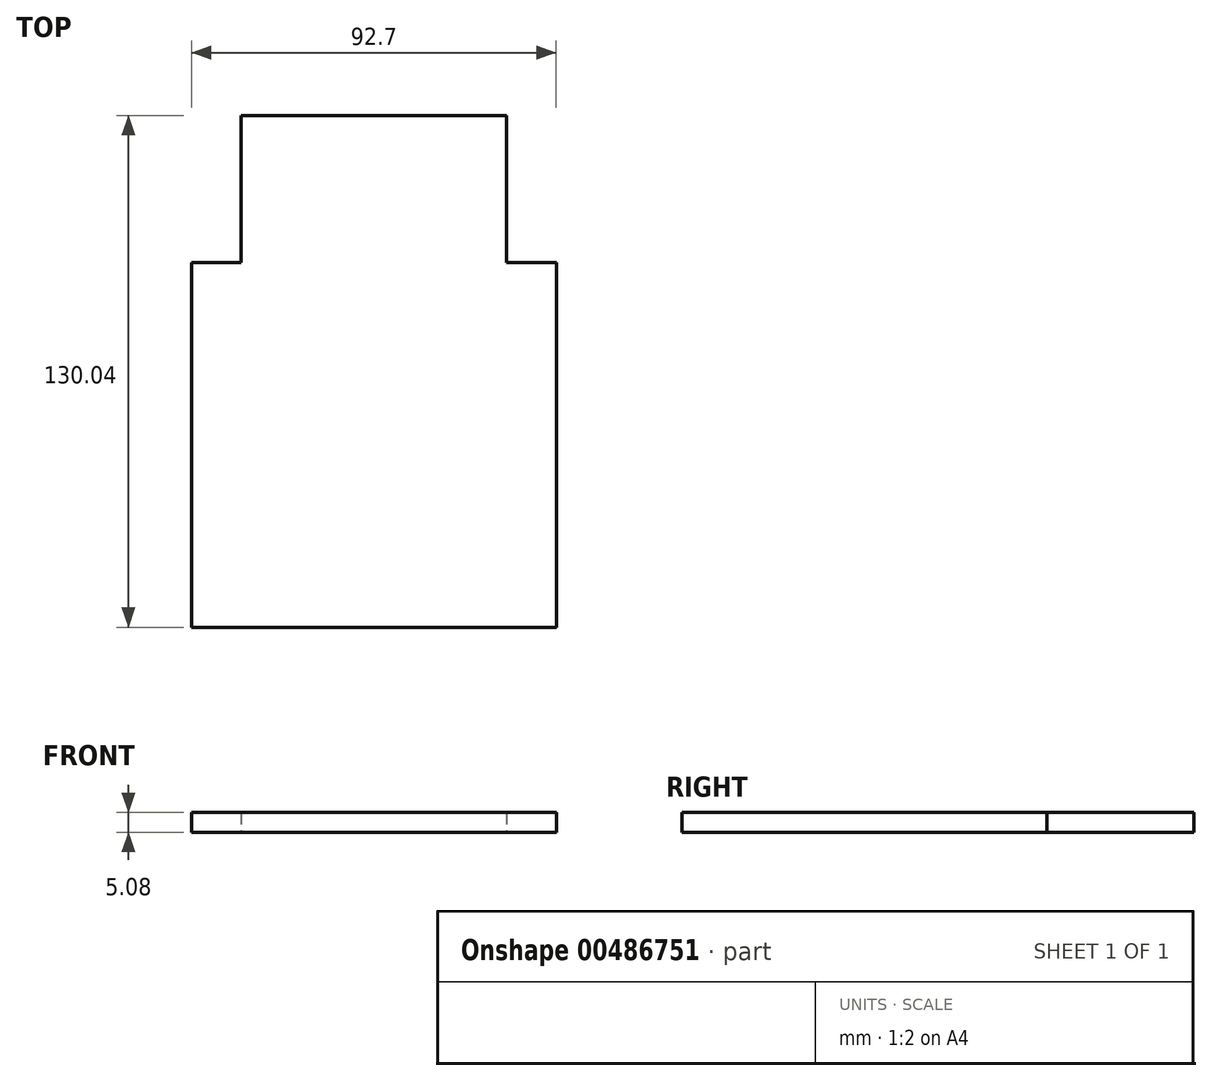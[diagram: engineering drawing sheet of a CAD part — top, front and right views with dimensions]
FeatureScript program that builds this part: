
annotation { "Feature Type Name" : "Feature", "Feature Type Description" : "" }
export const myFeature = defineFeature(function(context is Context, id is Id, definition is map)
    precondition{}
    {
        {
            var Q0;
            Q0=qCreatedBy(makeId("Top.planeOp"),FACE);
            var sketch = newSketch(context, id + "F0", { "sketchPlane" : qUnion([Q0])});
            skLineSegment(sketch, "E0.bottom", {"start": v(46.35, 46.35) * mm, "end": v(-46.35, 46.35) * mm});
            skLineSegment(sketch, "E0.top", {"start": v(46.36, -46.36) * mm, "end": v(-46.35, -46.36) * mm});
            skLineSegment(sketch, "E0.left", {"start": v(46.35, 46.35) * mm, "end": v(46.36, -46.36) * mm});
            skLineSegment(sketch, "E0.right", {"start": v(-46.35, 46.35) * mm, "end": v(-46.35, -46.36) * mm});
            skPoint(sketch, "E0.middle", {"position": v(0, 0) * mm});
            skLineSegment(sketch, "E1.bottom", {"start": v(33.73, 83.7) * mm, "end": v(-33.73, 83.7) * mm});
            skLineSegment(sketch, "E1.top", {"start": v(33.73, 9.02) * mm, "end": v(-33.73, 9.02) * mm});
            skLineSegment(sketch, "E1.left", {"start": v(33.73, 83.7) * mm, "end": v(33.73, 9.02) * mm});
            skLineSegment(sketch, "E1.right", {"start": v(-33.73, 83.7) * mm, "end": v(-33.73, 9.02) * mm});
            skPoint(sketch, "E1.middle", {"position": v(0, 46.35) * mm});
            skSolve(sketch);
        }
        {
            var Q0;
            Q0 = qSketchRegion(id + "F0", true);
            extrude(context, id + "F1", {"entities" : qUnion([Q0]), "depth" : 5.08 * mm, "offsetDistance" : 25.4 * mm});
        }
    });
